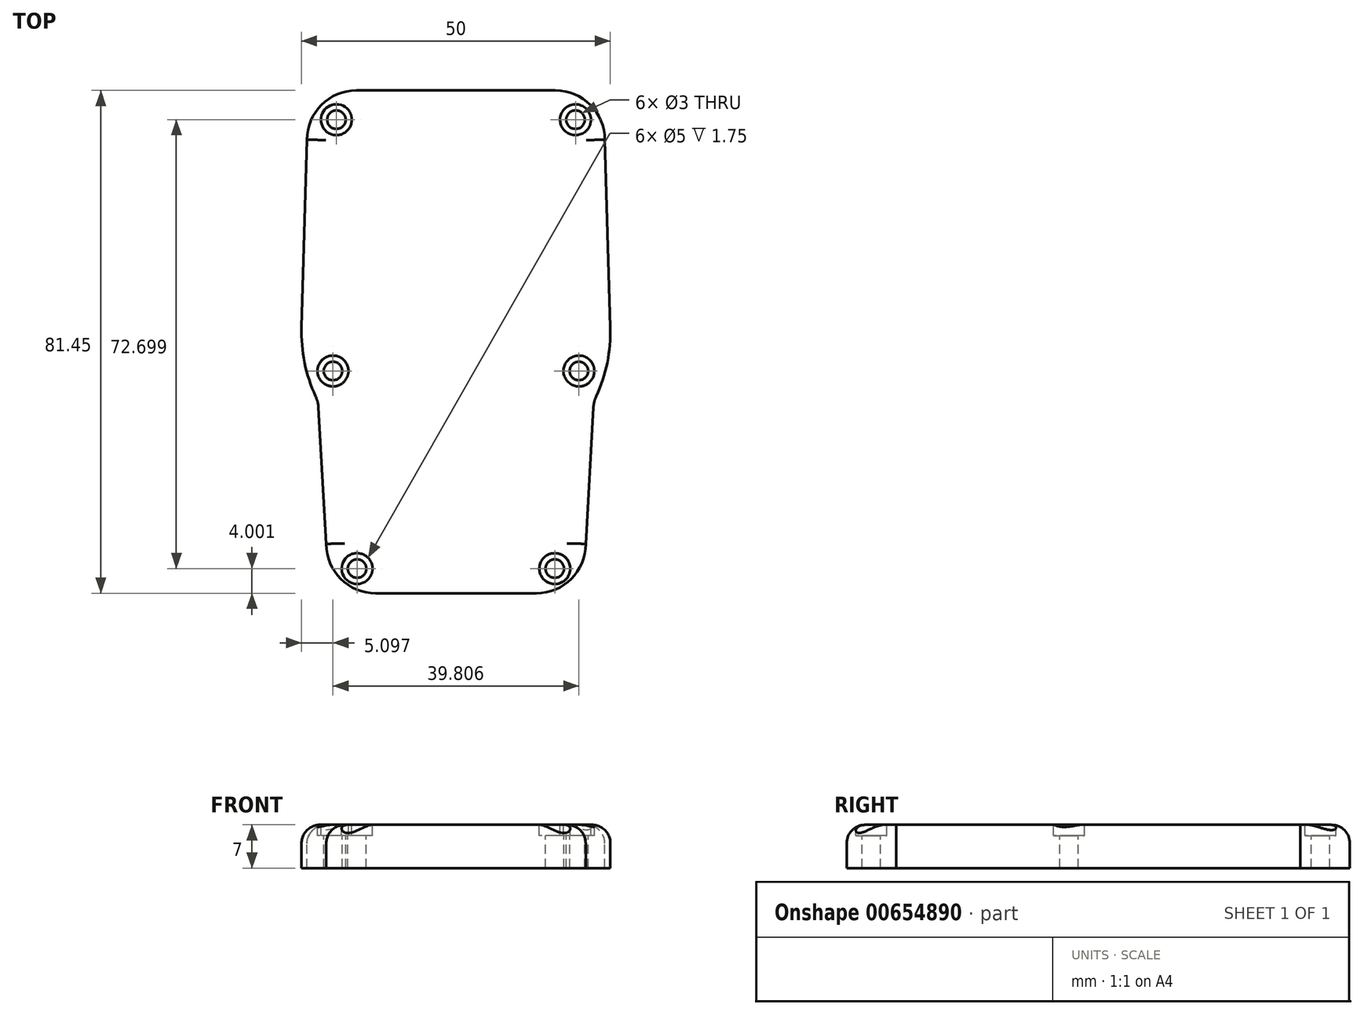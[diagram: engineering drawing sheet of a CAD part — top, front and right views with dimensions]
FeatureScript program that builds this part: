
annotation { "Feature Type Name" : "Feature", "Feature Type Description" : "" }
export const myFeature = defineFeature(function(context is Context, id is Id, definition is map)
    precondition{}
    {
        {
            var Q0;
            Q0=qCreatedBy(makeId("Top.planeOp"),FACE);
            var sketch = newSketch(context, id + "F0", { "sketchPlane" : qUnion([Q0])});
            skLineSegment(sketch, "E0.0", {"start": v(21, -34.35) * mm, "end": v(22.25, -12.28) * mm});
            skArc(sketch, "E0.1", {"start": v(13, -42.35) * mm, "mid": v(18.66, -40) * mm, "end": v(21, -34.35) * mm});
            skLineSegment(sketch, "E0.2", {"start": v(13, -42.35) * mm, "end": v(-13, -42.35) * mm});
            skLineSegment(sketch, "E0.3", {"start": v(-21, -34.35) * mm, "end": v(-22.25, -12.28) * mm});
            skArc(sketch, "E0.4", {"start": v(-21, -34.35) * mm, "mid": v(-18.66, -40) * mm, "end": v(-13, -42.35) * mm});
            skArc(sketch, "E0.5", {"start": v(-22.7, -10.47) * mm, "mid": v(-24.5, -5) * mm, "end": v(-24.99, 0.73) * mm});
            skArc(sketch, "E0.6", {"start": v(-22.7, -10.47) * mm, "mid": v(-22.4, -11.35) * mm, "end": v(-22.25, -12.28) * mm});
            skLineSegment(sketch, "E0.7", {"start": v(-24.1, 31.1) * mm, "end": v(-24.99, 0.73) * mm});
            skArc(sketch, "E0.8", {"start": v(-16.1, 39.1) * mm, "mid": v(-21.76, 36.76) * mm, "end": v(-24.1, 31.1) * mm});
            skLineSegment(sketch, "E0.9", {"start": v(16.1, 39.1) * mm, "end": v(-16.1, 39.1) * mm});
            skArc(sketch, "E0.10", {"start": v(24.1, 31.1) * mm, "mid": v(21.76, 36.76) * mm, "end": v(16.1, 39.1) * mm});
            skLineSegment(sketch, "E0.11", {"start": v(24.1, 31.1) * mm, "end": v(24.99, 0.73) * mm});
            skArc(sketch, "E0.12", {"start": v(24.99, 0.73) * mm, "mid": v(24.5, -5) * mm, "end": v(22.7, -10.47) * mm});
            skArc(sketch, "E0.13", {"start": v(22.25, -12.28) * mm, "mid": v(22.4, -11.35) * mm, "end": v(22.7, -10.47) * mm});
            skPoint(sketch, "E1", {"position": v(-19.35, 34.35) * mm});
            skPoint(sketch, "E2", {"position": v(19.35, 34.35) * mm});
            skPoint(sketch, "E3", {"position": v(19.9, -6.35) * mm});
            skPoint(sketch, "E4", {"position": v(-19.9, -6.35) * mm});
            skPoint(sketch, "E5", {"position": v(-16, -38.35) * mm});
            skPoint(sketch, "E6", {"position": v(16, -38.35) * mm});
            skCircle(sketch, "E7", {"center": v(-19.35, 34.35) * mm, "radius": 2.5 * mm});
            skCircle(sketch, "E8", {"center": v(19.35, 34.35) * mm, "radius": 2.5 * mm});
            skCircle(sketch, "E9", {"center": v(19.9, -6.35) * mm, "radius": 2.5 * mm});
            skCircle(sketch, "E10", {"center": v(-19.9, -6.35) * mm, "radius": 2.5 * mm});
            skCircle(sketch, "E11", {"center": v(-16, -38.35) * mm, "radius": 2.5 * mm});
            skCircle(sketch, "E12", {"center": v(16, -38.35) * mm, "radius": 2.5 * mm});
            skSolve(sketch);
        }
        {
            var Q0;
            Q0 = qSketchRegion(id + "F0", true);
            var Q1;
            Q1=makeQuery(id+"F0.imprint","IMPRINT",FACE,{"disambiguationData":[TD([[makeQuery(id+"F0.imprint","IMPRINT",EDGE,{"derivedFrom":sQuery(id+"F0.wireOp",EDGE,"E10")}),1.0]])]});
            var Q2;
            Q2=makeQuery(id+"F0.imprint","IMPRINT",FACE,{"disambiguationData":[TD([[makeQuery(id+"F0.imprint","IMPRINT",EDGE,{"derivedFrom":sQuery(id+"F0.wireOp",EDGE,"E11")}),1.0]])]});
            var Q3;
            Q3=makeQuery(id+"F0.imprint","IMPRINT",FACE,{"disambiguationData":[TD([[makeQuery(id+"F0.imprint","IMPRINT",EDGE,{"derivedFrom":sQuery(id+"F0.wireOp",EDGE,"E12")}),1.0]])]});
            var Q4;
            Q4=makeQuery(id+"F0.imprint","IMPRINT",FACE,{"disambiguationData":[TD([[makeQuery(id+"F0.imprint","IMPRINT",EDGE,{"derivedFrom":sQuery(id+"F0.wireOp",EDGE,"E9")}),1.0]])]});
            var Q5;
            Q5=makeQuery(id+"F0.imprint","IMPRINT",FACE,{"disambiguationData":[TD([[makeQuery(id+"F0.imprint","IMPRINT",EDGE,{"derivedFrom":sQuery(id+"F0.wireOp",EDGE,"E7")}),1.0]])]});
            var Q6;
            Q6=makeQuery(id+"F0.imprint","IMPRINT",FACE,{"disambiguationData":[TD([[makeQuery(id+"F0.imprint","IMPRINT",EDGE,{"derivedFrom":sQuery(id+"F0.wireOp",EDGE,"E8")}),1.0]])]});
            extrude(context, id + "F1", {"entities" : qUnion([Q0, Q1, Q2, Q3, Q4, Q5, Q6]), "oppositeDirection" : true, "depth" : 7 * mm, "offsetDistance" : 25 * mm});
        }
        {
            var Q0;
            Q0=sQuery(id+"F0.wireOp",VERTEX,"E1");
            var Q1;
            Q1=sQuery(id+"F0.wireOp",VERTEX,"E2");
            var Q2;
            Q2=sQuery(id+"F0.wireOp",VERTEX,"E3");
            var Q3;
            Q3=sQuery(id+"F0.wireOp",VERTEX,"E4");
            var Q4;
            Q4=sQuery(id+"F0.wireOp",VERTEX,"E5");
            var Q5;
            Q5=sQuery(id+"F0.wireOp",VERTEX,"E6");
            var Q6;
            Q6=makeQuery(id+"F1.opExtrude","SWEPT_BODY",BODY,{"disambiguationData":[OSD([sQuery(id+"F0.wireOp",EDGE,"E0.0"),sQuery(id+"F0.wireOp",EDGE,"E0.1"),sQuery(id+"F0.wireOp",EDGE,"E0.2"),sQuery(id+"F0.wireOp",EDGE,"E0.3"),sQuery(id+"F0.wireOp",EDGE,"E0.4"),sQuery(id+"F0.wireOp",EDGE,"E0.5"),sQuery(id+"F0.wireOp",EDGE,"E0.6"),sQuery(id+"F0.wireOp",EDGE,"E0.7"),sQuery(id+"F0.wireOp",EDGE,"E0.8"),sQuery(id+"F0.wireOp",EDGE,"E0.9"),sQuery(id+"F0.wireOp",EDGE,"E0.10"),sQuery(id+"F0.wireOp",EDGE,"E0.11"),sQuery(id+"F0.wireOp",EDGE,"E0.12"),sQuery(id+"F0.wireOp",EDGE,"E0.13")])]});
            hole(context, id + "F2", {"style" : HoleStyle.SIMPLE, "endStyle" : HoleEndStyle.BLIND, "holeDiameter" : 3 * mm, "majorDiameter" : 5 * mm, "holeDepth" : 12 * mm, "isTappedThrough" : true, "tappedDepth" : 12 * mm, "tapClearance" : 3, "locations" : qUnion([Q0, Q1, Q2, Q3, Q4, Q5]), "scope" : qUnion([Q6])});
        }
        {
            var Q0;
            Q0=makeQuery(id+"F0.imprint","IMPRINT",FACE,{"disambiguationData":[TD([[makeQuery(id+"F0.imprint","IMPRINT",EDGE,{"derivedFrom":sQuery(id+"F0.wireOp",EDGE,"E7")}),1.0]])]});
            var Q1;
            Q1=makeQuery(id+"F0.imprint","IMPRINT",FACE,{"disambiguationData":[TD([[makeQuery(id+"F0.imprint","IMPRINT",EDGE,{"derivedFrom":sQuery(id+"F0.wireOp",EDGE,"E8")}),1.0]])]});
            var Q2;
            Q2=makeQuery(id+"F0.imprint","IMPRINT",FACE,{"disambiguationData":[TD([[makeQuery(id+"F0.imprint","IMPRINT",EDGE,{"derivedFrom":sQuery(id+"F0.wireOp",EDGE,"E9")}),1.0]])]});
            var Q3;
            Q3=makeQuery(id+"F0.imprint","IMPRINT",FACE,{"disambiguationData":[TD([[makeQuery(id+"F0.imprint","IMPRINT",EDGE,{"derivedFrom":sQuery(id+"F0.wireOp",EDGE,"E10")}),1.0]])]});
            var Q4;
            Q4=makeQuery(id+"F0.imprint","IMPRINT",FACE,{"disambiguationData":[TD([[makeQuery(id+"F0.imprint","IMPRINT",EDGE,{"derivedFrom":sQuery(id+"F0.wireOp",EDGE,"E11")}),1.0]])]});
            var Q5;
            Q5=makeQuery(id+"F0.imprint","IMPRINT",FACE,{"disambiguationData":[TD([[makeQuery(id+"F0.imprint","IMPRINT",EDGE,{"derivedFrom":sQuery(id+"F0.wireOp",EDGE,"E12")}),1.0]])]});
            extrude(context, id + "F3", {"entities" : qUnion([Q0, Q1, Q2, Q3, Q4, Q5]), "operationType" : NewBodyOperationType.REMOVE, "oppositeDirection" : true, "depth" : 1.75 * mm, "offsetDistance" : 25 * mm});
        }
        {
            var Q0;
            Q0=makeQuery(id+"F1.opExtrude","CAP_EDGE",EDGE,{"disambiguationData":[OSD([sQuery(id+"F0.wireOp",EDGE,"E0.4")])],"isStart":true});
            var Q1;
            Q1=makeQuery(id+"F1.opExtrude","CAP_EDGE",EDGE,{"disambiguationData":[OSD([sQuery(id+"F0.wireOp",EDGE,"E0.11")])],"isStart":true});
            var Q2;
            Q2=makeQuery(id+"F1.opExtrude","CAP_EDGE",EDGE,{"disambiguationData":[OSD([sQuery(id+"F0.wireOp",EDGE,"E0.7")])],"isStart":true});
            var Q3;
            Q3=makeQuery(id+"F1.opExtrude","CAP_EDGE",EDGE,{"disambiguationData":[OSD([sQuery(id+"F0.wireOp",EDGE,"E0.9")])],"isStart":true});
            fillet(context, id + "F4", {"entities" : qUnion([Q0, Q1, Q2, Q3]), "radius" : 3 * mm, "tangentPropagation" : true, "allowEdgeOverflow" : false});
        }
    });
